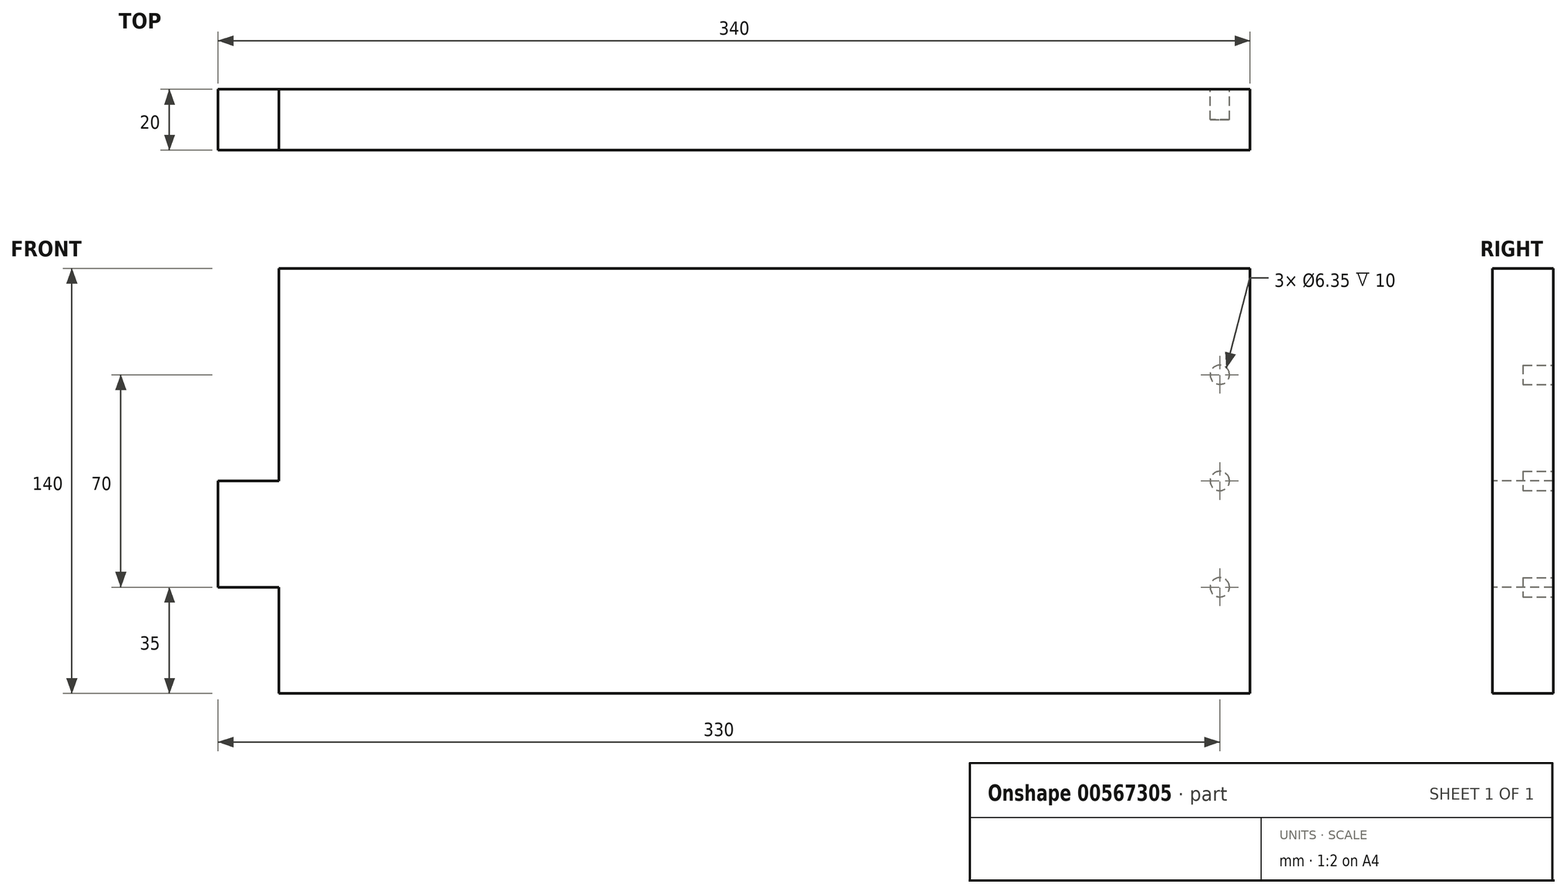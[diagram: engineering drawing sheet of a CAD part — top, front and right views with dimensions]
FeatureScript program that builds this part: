
annotation { "Feature Type Name" : "Feature", "Feature Type Description" : "" }
export const myFeature = defineFeature(function(context is Context, id is Id, definition is map)
    precondition{}
    {
        {
            var Q0;
            Q0=qCreatedBy(makeId("Front.planeOp"),FACE);
            var sketch = newSketch(context, id + "F0", { "sketchPlane" : qUnion([Q0])});
            skLineSegment(sketch, "E0.bottom", {"start": v(170, 70) * mm, "end": v(-170, 70) * mm});
            skLineSegment(sketch, "E0.top", {"start": v(170, -70) * mm, "end": v(-170, -70) * mm});
            skLineSegment(sketch, "E0.left", {"start": v(170, 70) * mm, "end": v(170, -70) * mm});
            skLineSegment(sketch, "E0.right", {"start": v(-170, 70) * mm, "end": v(-170, -70) * mm});
            skPoint(sketch, "E0.middle", {"position": v(0, 0) * mm});
            skLineSegment(sketch, "E1.bottom", {"start": v(-170, 70) * mm, "end": v(-150, 70) * mm});
            skLineSegment(sketch, "E1.top", {"start": v(-170, -70) * mm, "end": v(-150, -70) * mm});
            skLineSegment(sketch, "E1.right", {"start": v(-150, 70) * mm, "end": v(-150, -70) * mm});
            skLineSegment(sketch, "E2.top", {"start": v(-170, 35) * mm, "end": v(-150, 35) * mm});
            skLineSegment(sketch, "E2.left", {"start": v(-170, 70) * mm, "end": v(-170, 35) * mm});
            skLineSegment(sketch, "E2.right", {"start": v(-150, 70) * mm, "end": v(-150, 35) * mm});
            skLineSegment(sketch, "E3.top", {"start": v(-170, 0) * mm, "end": v(-150, 0) * mm});
            skLineSegment(sketch, "E3.left", {"start": v(-170, 35) * mm, "end": v(-170, 0) * mm});
            skLineSegment(sketch, "E3.right", {"start": v(-150, 35) * mm, "end": v(-150, 0) * mm});
            skLineSegment(sketch, "E4.top", {"start": v(-170, -35) * mm, "end": v(-150, -35) * mm});
            skLineSegment(sketch, "E4.left", {"start": v(-170, 0) * mm, "end": v(-170, -35) * mm});
            skLineSegment(sketch, "E4.right", {"start": v(-150, 0) * mm, "end": v(-150, -35) * mm});
            skLineSegment(sketch, "E5.left", {"start": v(-170, -35) * mm, "end": v(-170, -70) * mm});
            skLineSegment(sketch, "E5.right", {"start": v(-150, -35) * mm, "end": v(-150, -70) * mm});
            skLineSegment(sketch, "E6.bottom", {"start": v(170, 70) * mm, "end": v(150, 70) * mm});
            skLineSegment(sketch, "E6.top", {"start": v(170, -70) * mm, "end": v(150, -70) * mm});
            skPoint(sketch, "E7.center.orphan", {"position": v(160, 35) * mm});
            skPoint(sketch, "E8.end.orphan", {"position": v(170, 35) * mm});
            skPoint(sketch, "E9.orphan", {"position": v(150, 35) * mm});
            skPoint(sketch, "E10.center.orphan", {"position": v(160, 0) * mm});
            skPoint(sketch, "E11.end.orphan", {"position": v(170, 0) * mm});
            skPoint(sketch, "E12.start.orphan", {"position": v(150, 0) * mm});
            skPoint(sketch, "E13.start.orphan", {"position": v(150, -35) * mm});
            skPoint(sketch, "E14.trimOffspring.end.orphan", {"position": v(170, -35) * mm});
            skPoint(sketch, "E14.trimOffspring.start.orphan", {"position": v(160, -35) * mm});
            skSolve(sketch);
        }
        {
            var Q0;
            Q0=makeQuery(id+"F0.imprint","IMPRINT",FACE,{"disambiguationData":[TD([[makeQuery(id+"F0.imprint","IMPRINT",EDGE,{"derivedFrom":sQuery(id+"F0.wireOp",EDGE,"E1.bottom")}),-1.0]])]});
            var Q1;
            Q1=makeQuery(id+"F0.imprint","IMPRINT",FACE,{"disambiguationData":[TD([[makeQuery(id+"F0.imprint","IMPRINT",EDGE,{"derivedFrom":sQuery(id+"F0.wireOp",EDGE,"E3.top")}),-1.0]])]});
            var Q2;
            Q2=makeQuery(id+"F0.imprint","IMPRINT",FACE,{"disambiguationData":[TD([[makeQuery(id+"F0.imprint","IMPRINT",EDGE,{"derivedFrom":sQuery(id+"F0.wireOp",EDGE,"E0.bottom")}),1.0]])]});
            var Q3;
            {var subQ7=sQuery(id+"F0.wireOp",EDGE,"E6.bottom");Q3=makeQuery(id+"F0.imprint","IMPRINT",FACE,{"disambiguationData":[TD([[makeQuery(id+"F0.imprint","IMPRINT",EDGE,{"derivedFrom":subQ7}),1.0]])]});}
            var Q4;
            {var subQ0=sQuery(id+"F0.wireOp",EDGE,"E7");var subQ1=sQuery(id+"F0.wireOp",EDGE,"E8");var subQ2=makeQuery(id+"F0.imprint","INTERSECT",VERTEX,{"disambiguationData":[OD(0.0)],"derivedFrom":[subQ1,subQ0]});Q4=makeQuery(id+"F0.imprint","IMPRINT",FACE,{"disambiguationData":[TD([[makeQuery(id+"F0.imprint","IMPRINT",EDGE,{"disambiguationData":[TD([[subQ2,-1.0]])],"derivedFrom":subQ1}),-1.0]])]});}
            var Q5;
            {var subQ0=sQuery(id+"F0.wireOp",EDGE,"E7");var subQ1=sQuery(id+"F0.wireOp",EDGE,"E8");var subQ2=makeQuery(id+"F0.imprint","INTERSECT",VERTEX,{"disambiguationData":[OD(0.0)],"derivedFrom":[subQ1,subQ0]});Q5=makeQuery(id+"F0.imprint","IMPRINT",FACE,{"disambiguationData":[TD([[makeQuery(id+"F0.imprint","IMPRINT",EDGE,{"disambiguationData":[TD([[subQ2,-1.0]])],"derivedFrom":subQ1}),1.0]])]});}
            var Q6;
            {var subQ0=sQuery(id+"F0.wireOp",EDGE,"LQTl8Tgs-W7DE-Rj0l-Qspb-1fxBIX7TMnu1");Q6=makeQuery(id+"F0.imprint","IMPRINT",FACE,{"disambiguationData":[TD([[makeQuery(id+"F0.imprint","IMPRINT",EDGE,{"derivedFrom":subQ0}),-1.0]])]});}
            var Q7;
            {var subQ0=sQuery(id+"F0.wireOp",EDGE,"EbxZGf6J-t8Ci-gmo8-XZhK-rdHW3A5GWB9B");Q7=makeQuery(id+"F0.imprint","IMPRINT",FACE,{"disambiguationData":[TD([[makeQuery(id+"F0.imprint","IMPRINT",EDGE,{"derivedFrom":subQ0}),1.0]])]});}
            var Q8;
            {var subQ1=sQuery(id+"F0.wireOp",EDGE,"E6.top");Q8=makeQuery(id+"F0.imprint","IMPRINT",FACE,{"disambiguationData":[TD([[makeQuery(id+"F0.imprint","IMPRINT",EDGE,{"derivedFrom":subQ1}),-1.0]])]});}
            var Q9;
            {var subQ0=sQuery(id+"F0.wireOp",EDGE,"h3PSeiwS-uXRa-Lzge-hjhJ-VVAhPI6omThI");var subQ1=sQuery(id+"F0.wireOp",EDGE,"E13");var subQ2=makeQuery(id+"F0.imprint","INTERSECT",VERTEX,{"disambiguationData":[OD(0.0)],"derivedFrom":[subQ1,subQ0]});Q9=makeQuery(id+"F0.imprint","IMPRINT",FACE,{"disambiguationData":[TD([[makeQuery(id+"F0.imprint","IMPRINT",EDGE,{"disambiguationData":[TD([[subQ2,-1.0]])],"derivedFrom":subQ1}),-1.0]])]});}
            var Q10;
            {var subQ0=sQuery(id+"F0.wireOp",EDGE,"h3PSeiwS-uXRa-Lzge-hjhJ-VVAhPI6omThI");var subQ1=sQuery(id+"F0.wireOp",EDGE,"E13");var subQ2=makeQuery(id+"F0.imprint","INTERSECT",VERTEX,{"disambiguationData":[OD(0.0)],"derivedFrom":[subQ1,subQ0]});Q10=makeQuery(id+"F0.imprint","IMPRINT",FACE,{"disambiguationData":[TD([[makeQuery(id+"F0.imprint","IMPRINT",EDGE,{"disambiguationData":[TD([[subQ2,-1.0]])],"derivedFrom":subQ1}),1.0]])]});}
            var Q11;
            {var subQ0=sQuery(id+"F0.wireOp",EDGE,"E10");var subQ1=sQuery(id+"F0.wireOp",EDGE,"E11");var subQ2=makeQuery(id+"F0.imprint","INTERSECT",VERTEX,{"disambiguationData":[OD(0.0)],"derivedFrom":[subQ1,subQ0]});Q11=makeQuery(id+"F0.imprint","IMPRINT",FACE,{"disambiguationData":[TD([[makeQuery(id+"F0.imprint","IMPRINT",EDGE,{"disambiguationData":[TD([[subQ2,-1.0]])],"derivedFrom":subQ1}),-1.0]])]});}
            var Q12;
            {var subQ0=sQuery(id+"F0.wireOp",EDGE,"E10");var subQ1=sQuery(id+"F0.wireOp",EDGE,"E11");var subQ2=makeQuery(id+"F0.imprint","INTERSECT",VERTEX,{"disambiguationData":[OD(0.0)],"derivedFrom":[subQ1,subQ0]});Q12=makeQuery(id+"F0.imprint","IMPRINT",FACE,{"disambiguationData":[TD([[makeQuery(id+"F0.imprint","IMPRINT",EDGE,{"disambiguationData":[TD([[subQ2,-1.0]])],"derivedFrom":subQ1}),1.0]])]});}
            extrude(context, id + "F1", {"entities" : qUnion([Q0, Q1, Q2, Q3, Q4, Q5, Q6, Q7, Q8, Q9, Q10, Q11, Q12]), "oppositeDirection" : true, "depth" : 20 * mm, "offsetDistance" : 25.4 * mm});
        }
        {
            var Q0;
            Q0=makeQuery(id+"F1.opExtrude","CAP_FACE",FACE,{"disambiguationData":[OSD([sQuery(id+"F0.wireOp",EDGE,"E0.bottom"),sQuery(id+"F0.wireOp",EDGE,"E0.top"),sQuery(id+"F0.wireOp",EDGE,"E0.left"),sQuery(id+"F0.wireOp",EDGE,"E1.bottom"),sQuery(id+"F0.wireOp",EDGE,"E2.left"),sQuery(id+"F0.wireOp",EDGE,"E2.top"),sQuery(id+"F0.wireOp",EDGE,"E3.right"),sQuery(id+"F0.wireOp",EDGE,"E3.top"),sQuery(id+"F0.wireOp",EDGE,"E4.left"),sQuery(id+"F0.wireOp",EDGE,"E4.top"),sQuery(id+"F0.wireOp",EDGE,"E5.right")])],"isStart":false});
            var sketch = newSketch(context, id + "F2", { "sketchPlane" : qUnion([Q0])});
            skLineSegment(sketch, "E15", {"start": v(160, 0) * mm, "end": v(160, -35) * mm});
            skSolve(sketch);
        }
        {
            var Q0;
            {var subQ2=sQuery(id+"F2.wireOp",EDGE,"E15");Q0=makeQuery(id+"F2.imprint","IMPRINT",FACE,{"disambiguationData":[TD([[makeQuery(id+"F2.imprint","IMPRINT",EDGE,{"derivedFrom":subQ2}),-1.0]])]});}
            var sketch = newSketch(context, id + "F3", { "sketchPlane" : qUnion([Q0])});
            skCircle(sketch, "E16", {"center": v(-160, 35) * mm, "radius": 3.17 * mm});
            skCircle(sketch, "E17", {"center": v(-160, 0) * mm, "radius": 3.18 * mm});
            skCircle(sketch, "E18", {"center": v(-160, -35) * mm, "radius": 3.18 * mm});
            skSolve(sketch);
        }
        {
            var Q0;
            Q0 = qSketchRegion(id + "F3", true);
            extrude(context, id + "F4", {"entities" : qUnion([Q0]), "operationType" : NewBodyOperationType.REMOVE, "oppositeDirection" : true, "depth" : 10 * mm, "offsetDistance" : 25 * mm});
        }
    });
